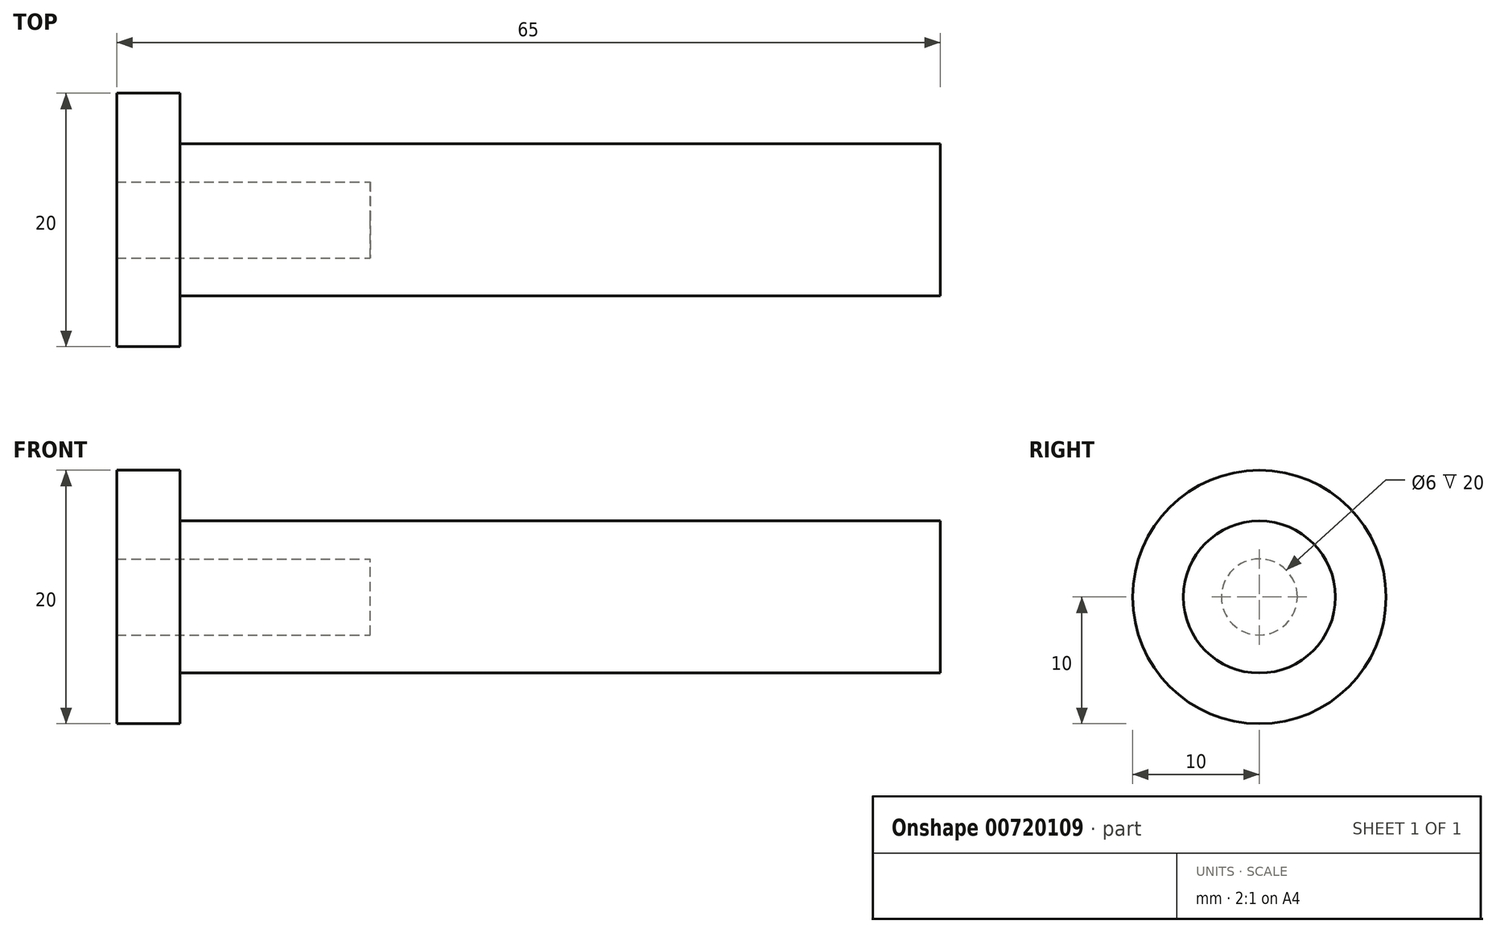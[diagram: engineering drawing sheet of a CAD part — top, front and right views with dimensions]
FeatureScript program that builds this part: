
annotation { "Feature Type Name" : "Feature", "Feature Type Description" : "" }
export const myFeature = defineFeature(function(context is Context, id is Id, definition is map)
    precondition{}
    {
        {
            var Q0;
            Q0=qCreatedBy(makeId("Front.planeOp"),FACE);
            var sketch = newSketch(context, id + "F0", { "sketchPlane" : qUnion([Q0])});
            skLineSegment(sketch, "E0", {"start": v(0, 3) * mm, "end": v(0, 10) * mm});
            skLineSegment(sketch, "E1", {"start": v(0, 10) * mm, "end": v(5, 10) * mm});
            skLineSegment(sketch, "E2", {"start": v(5, 10) * mm, "end": v(5, 6) * mm});
            skLineSegment(sketch, "E3", {"start": v(5, 6) * mm, "end": v(65, 6) * mm});
            skLineSegment(sketch, "E4.0", {"start": v(20, 3) * mm, "end": v(0, 3) * mm});
            skLineSegment(sketch, "E5.0", {"start": v(20, 0) * mm, "end": v(20, 3) * mm});
            skPoint(sketch, "E6.orphan", {"position": v(0, 0) * mm});
            skLineSegment(sketch, "E7", {"start": v(65, 6) * mm, "end": v(65, 0) * mm});
            skLineSegment(sketch, "E8", {"start": v(65, 0) * mm, "end": v(20, 0) * mm});
            skSolve(sketch);
        }
        {
            var Q0;
            Q0=makeQuery(id+"F0.imprint","IMPRINT",FACE,{"disambiguationData":[TD([[makeQuery(id+"F0.imprint","IMPRINT",EDGE,{"derivedFrom":sQuery(id+"F0.wireOp",EDGE,"E0")}),-1.0]])]});
            var Q1;
            Q1=sQuery(id+"F0.wireOp",EDGE,"E8");
            revolve(context, id + "F1", {"surfaceOperationType" : NewSurfaceOperationType.NEW, "entities" : qUnion([Q0]), "axis" : qUnion([Q1]), "revolveType" : RevolveType.FULL});
        }
    });
